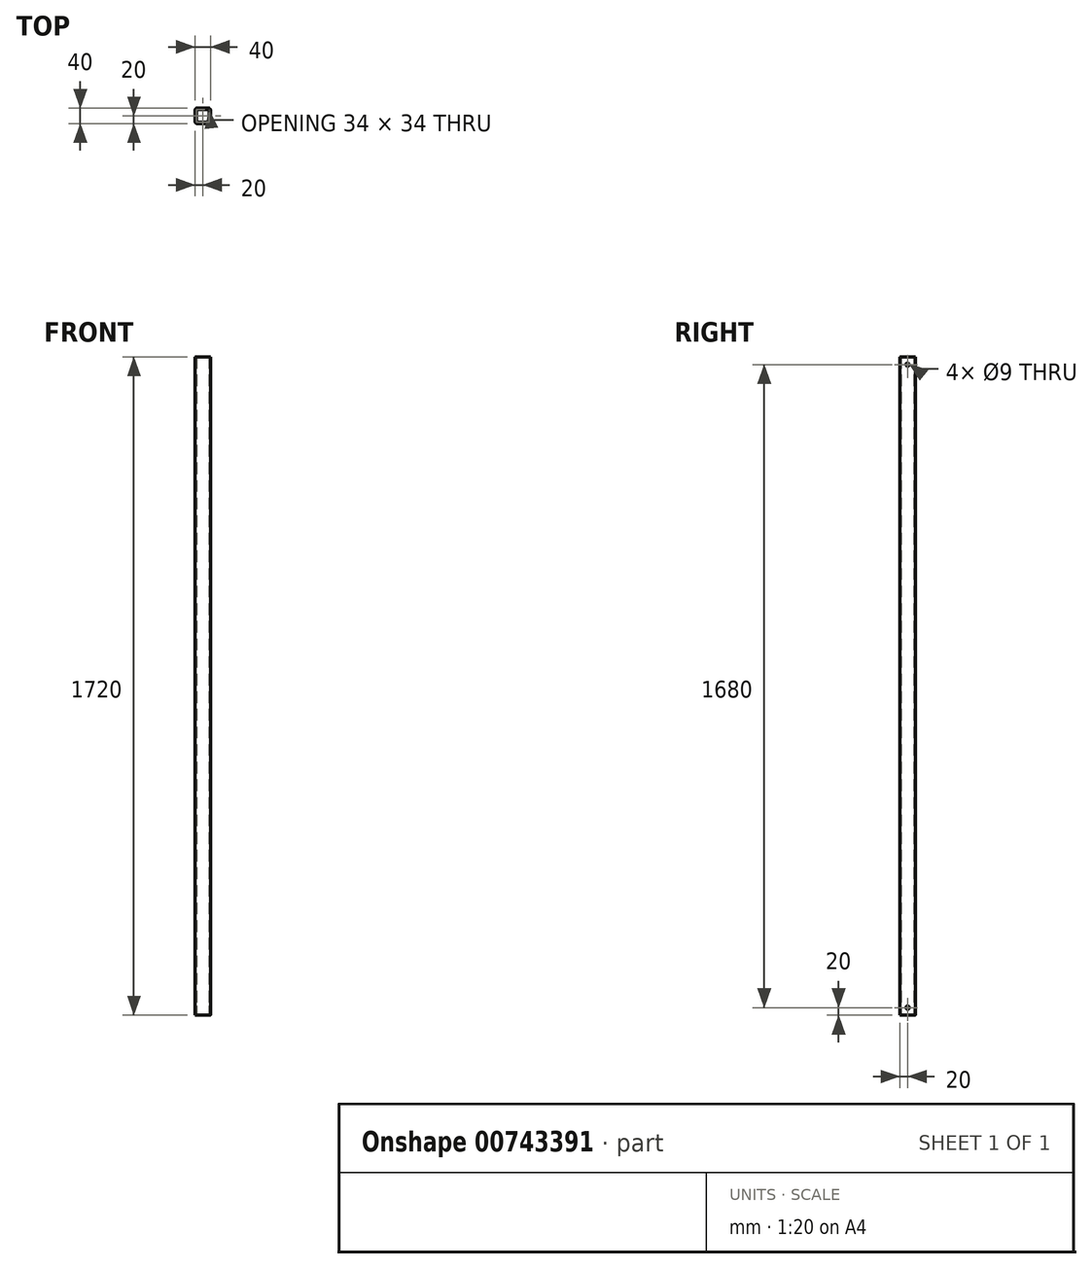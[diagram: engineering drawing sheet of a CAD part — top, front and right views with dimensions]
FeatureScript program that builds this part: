
annotation { "Feature Type Name" : "Feature", "Feature Type Description" : "" }
export const myFeature = defineFeature(function(context is Context, id is Id, definition is map)
    precondition{}
    {
        {
            var Q0;
            Q0=qCreatedBy(makeId("Top.planeOp"),FACE);
            var sketch = newSketch(context, id + "F0", { "sketchPlane" : qUnion([Q0])});
            skLineSegment(sketch, "E0.bottom", {"start": v(15.5, -20) * mm, "end": v(-15.5, -20) * mm});
            skLineSegment(sketch, "E0.top", {"start": v(15.5, 20) * mm, "end": v(-15.5, 20) * mm});
            skLineSegment(sketch, "E0.left", {"start": v(20, -15.5) * mm, "end": v(20, 15.5) * mm});
            skLineSegment(sketch, "E0.right", {"start": v(-20, -15.5) * mm, "end": v(-20, 15.5) * mm});
            skPoint(sketch, "E0.middle", {"position": v(0, 0) * mm});
            skPoint(sketch, "E1.visualSharp", {"position": v(-20, 20) * mm});
            skArc(sketch, "E2.filletArc", {"start": v(-15.5, 20) * mm, "mid": v(-18.68, 18.68) * mm, "end": v(-20, 15.5) * mm});
            skPoint(sketch, "E3.visualSharp", {"position": v(20, 20) * mm});
            skArc(sketch, "E3.filletArc", {"start": v(20, 15.5) * mm, "mid": v(18.68, 18.68) * mm, "end": v(15.5, 20) * mm});
            skPoint(sketch, "E4.visualSharp", {"position": v(20, -20) * mm});
            skArc(sketch, "E4.filletArc", {"start": v(15.5, -20) * mm, "mid": v(18.68, -18.68) * mm, "end": v(20, -15.5) * mm});
            skPoint(sketch, "E5.visualSharp", {"position": v(-20, -20) * mm});
            skArc(sketch, "E5.filletArc", {"start": v(-20, -15.5) * mm, "mid": v(-18.68, -18.68) * mm, "end": v(-15.5, -20) * mm});
            skArc(sketch, "E6.0", {"start": v(17, 15.5) * mm, "mid": v(16.56, 16.56) * mm, "end": v(15.5, 17) * mm});
            skLineSegment(sketch, "E6.1", {"start": v(17, -15.5) * mm, "end": v(17, 15.5) * mm});
            skLineSegment(sketch, "E6.2", {"start": v(15.5, 17) * mm, "end": v(-15.5, 17) * mm});
            skArc(sketch, "E6.3", {"start": v(15.5, -17) * mm, "mid": v(16.56, -16.56) * mm, "end": v(17, -15.5) * mm});
            skArc(sketch, "E6.4", {"start": v(-15.5, 17) * mm, "mid": v(-16.56, 16.56) * mm, "end": v(-17, 15.5) * mm});
            skLineSegment(sketch, "E6.5", {"start": v(-17, -15.5) * mm, "end": v(-17, 15.5) * mm});
            skArc(sketch, "E6.6", {"start": v(-17, -15.5) * mm, "mid": v(-16.56, -16.56) * mm, "end": v(-15.5, -17) * mm});
            skLineSegment(sketch, "E6.7", {"start": v(15.5, -17) * mm, "end": v(-15.5, -17) * mm});
            skSolve(sketch);
        }
        {
            var Q0;
            Q0 = qSketchRegion(id + "F0", true);
            extrude(context, id + "F1", {"entities" : qUnion([Q0]), "depth" : 1720 * mm, "offsetDistance" : 25 * mm});
        }
        {
            var Q0;
            Q0=makeQuery(id+"F1.opExtrude","SWEPT_FACE",FACE,{"disambiguationData":[OSD([sQuery(id+"F0.wireOp",EDGE,"E0.left")])]});
            var sketch = newSketch(context, id + "F2", { "sketchPlane" : qUnion([Q0])});
            skLineSegment(sketch, "E7", {"start": v(0, 0) * mm, "end": v(0, 1720) * mm, "construction": true});
            skCircle(sketch, "E8", {"center": v(0, 1700) * mm, "radius": 4.5 * mm});
            skCircle(sketch, "E9", {"center": v(0, 20) * mm, "radius": 4.5 * mm});
            skSolve(sketch);
        }
        {
            var Q0;
            Q0 = qSketchRegion(id + "F2", true);
            extrude(context, id + "F3", {"entities" : qUnion([Q0]), "operationType" : NewBodyOperationType.REMOVE, "endBound" : BoundingType.THROUGH_ALL, "oppositeDirection" : true, "depth" : 25 * mm, "offsetDistance" : 25 * mm});
        }
    });
